# Revit family: Gira_129600
name_source: partatom
category: Electrical Fixtures
revit_build: Autodesk Revit 2017 (Build: 20160225_1515(x64)
units: mm (PartAtom-declared; Revit-internal decimal feet)

## family parameters
Cut with Voids When Loaded = No
Host = Face
Maintain Annotation Orientation = No
Part Type = Normal
Room Calculation Point = No
Round Connector Dimension = Use Diameter
Shared = No

## types (1)
- Pow.supply DC 24 V 300 mA DRA Door communication
    BIM = https://media.live.bim.site 00_REG 6.rfa
    BIMSITE_PRODUCT_ID = 21df1e56c7accd880677f37bc9f96e8d9aef7743
    Cost = 0 $
    Default Elevation = 1219 mm
    Description = PS DC 24V 300mA DRA Door Power supply for door communication DC 24 V 300 mA,DRA Features: - Power supply DC 24 V to supply power to the door communication components. - Power supply to the colour camera in large properties. - Power supply to the call-button illumination in large properties. - Power supply to the DCS-TC gateway when the video control device is used. - Supply of Keyless In keypad.
    GTIN = 4010337296003
    HAN = 129600
    HeinzeBIM = https://www.heinze.de
    Manufacturer = Gira
    Output voltage [Volt] Number = 24
    URL = https://www.gira.de

## geometry (parser evidence)
native form markers: Blend x2, Sweep x2
no freeform markers — native parametric forms only
